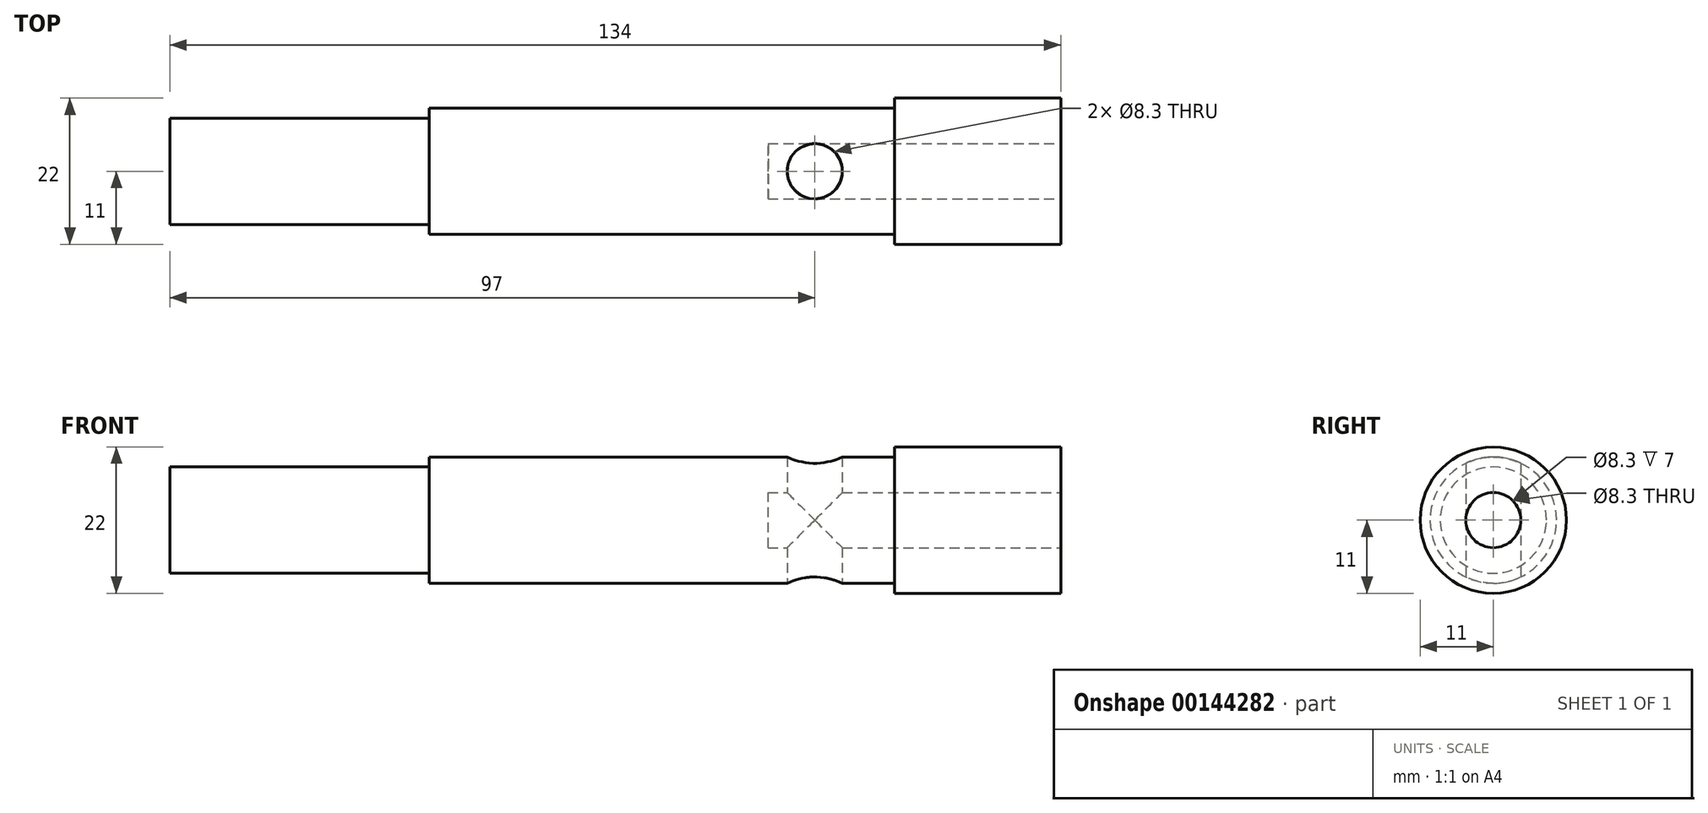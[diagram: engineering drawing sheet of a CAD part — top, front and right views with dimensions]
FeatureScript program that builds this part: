
annotation { "Feature Type Name" : "Feature", "Feature Type Description" : "" }
export const myFeature = defineFeature(function(context is Context, id is Id, definition is map)
    precondition{}
    {
        {
            var Q0;
            Q0=qCreatedBy(makeId("Front.planeOp"),FACE);
            var sketch = newSketch(context, id + "F0", { "sketchPlane" : qUnion([Q0])});
            skLineSegment(sketch, "E0", {"start": v(-58.13, 0) * mm, "end": v(0, 0) * mm, "construction": true});
            skLineSegment(sketch, "E1.bottom", {"start": v(0, 0) * mm, "end": v(-25, 0) * mm});
            skLineSegment(sketch, "E1.top", {"start": v(0, 11) * mm, "end": v(-25, 11) * mm});
            skLineSegment(sketch, "E1.left", {"start": v(0, 0) * mm, "end": v(0, 11) * mm});
            skLineSegment(sketch, "E1.right", {"start": v(-25, 0) * mm, "end": v(-25, 11) * mm});
            skLineSegment(sketch, "E2.bottom", {"start": v(-25, 0) * mm, "end": v(-37, 0) * mm});
            skLineSegment(sketch, "E2.top", {"start": v(-25, 9.5) * mm, "end": v(-37, 9.5) * mm});
            skLineSegment(sketch, "E2.left", {"start": v(-25, 0) * mm, "end": v(-25, 9.5) * mm});
            skLineSegment(sketch, "E2.right", {"start": v(-37, 0) * mm, "end": v(-37, 9.5) * mm});
            skLineSegment(sketch, "E3.bottom", {"start": v(-37, 0) * mm, "end": v(-95, 0) * mm});
            skLineSegment(sketch, "E3.top", {"start": v(-37, 9.5) * mm, "end": v(-95, 9.5) * mm});
            skLineSegment(sketch, "E3.right", {"start": v(-95, 0) * mm, "end": v(-95, 9.5) * mm});
            skLineSegment(sketch, "E4.bottom", {"start": v(-95, 0) * mm, "end": v(-134, 0) * mm});
            skLineSegment(sketch, "E4.top", {"start": v(-95, 8) * mm, "end": v(-134, 8) * mm});
            skLineSegment(sketch, "E4.left", {"start": v(-95, 0) * mm, "end": v(-95, 8) * mm});
            skLineSegment(sketch, "E4.right", {"start": v(-134, 0) * mm, "end": v(-134, 8) * mm});
            skLineSegment(sketch, "E5.MirrorCS", {"start": v(-25, 0) * mm, "end": v(-25, -11) * mm});
            skLineSegment(sketch, "E6.MirrorCS", {"start": v(-37, 0) * mm, "end": v(-37, -9.5) * mm});
            skLineSegment(sketch, "E7.MirrorCS", {"start": v(-95, 0) * mm, "end": v(-95, -8) * mm});
            skLineSegment(sketch, "E8.MirrorCS", {"start": v(-134, 0) * mm, "end": v(-134, -8) * mm});
            skLineSegment(sketch, "E9.MirrorCS", {"start": v(-95, 0) * mm, "end": v(-95, -9.5) * mm});
            skLineSegment(sketch, "E10.MirrorCS", {"start": v(-37, -9.5) * mm, "end": v(-95, -9.5) * mm});
            skLineSegment(sketch, "E11.MirrorCS", {"start": v(-25, 0) * mm, "end": v(-25, -9.5) * mm});
            skLineSegment(sketch, "E12.MirrorCS", {"start": v(-25, -9.5) * mm, "end": v(-37, -9.5) * mm});
            skLineSegment(sketch, "E13.MirrorCS", {"start": v(0, 0) * mm, "end": v(0, -11) * mm});
            skLineSegment(sketch, "E14.MirrorCS", {"start": v(0, -11) * mm, "end": v(-25, -11) * mm});
            skLineSegment(sketch, "E15.MirrorCS", {"start": v(-95, -8) * mm, "end": v(-134, -8) * mm});
            skSolve(sketch);
        }
        {
            var Q0;
            Q0=makeQuery(id+"F0.imprint","IMPRINT",FACE,{"disambiguationData":[TD([[makeQuery(id+"F0.imprint","IMPRINT",EDGE,{"derivedFrom":sQuery(id+"F0.wireOp",EDGE,"E1.bottom")}),-1.0]])]});
            var Q1;
            Q1=makeQuery(id+"F0.imprint","IMPRINT",FACE,{"disambiguationData":[TD([[makeQuery(id+"F0.imprint","IMPRINT",EDGE,{"derivedFrom":sQuery(id+"F0.wireOp",EDGE,"E2.top")}),1.0]])]});
            var Q2;
            Q2=makeQuery(id+"F0.imprint","IMPRINT",FACE,{"disambiguationData":[TD([[makeQuery(id+"F0.imprint","IMPRINT",EDGE,{"derivedFrom":sQuery(id+"F0.wireOp",EDGE,"E3.top")}),1.0]])]});
            var Q3;
            Q3=makeQuery(id+"F0.imprint","IMPRINT",FACE,{"disambiguationData":[TD([[makeQuery(id+"F0.imprint","IMPRINT",EDGE,{"derivedFrom":sQuery(id+"F0.wireOp",EDGE,"E4.top")}),1.0]])]});
            var Q4;
            Q4=sQuery(id+"F0.wireOp",EDGE,"E1.bottom");
            revolve(context, id + "F1", {"entities" : qUnion([Q0, Q1, Q2, Q3]), "axis" : qUnion([Q4]), "revolveType" : RevolveType.FULL});
        }
        {
            var Q0;
            Q0=qCreatedBy(makeId("Top.planeOp"),FACE);
            var sketch = newSketch(context, id + "F2", { "sketchPlane" : qUnion([Q0])});
            skLineSegment(sketch, "E16.0", {"start": v(-37, 0) * mm, "end": v(-95, 0) * mm});
            skLineSegment(sketch, "E17.0", {"start": v(-25, 0) * mm, "end": v(-37, 0) * mm});
            skCircle(sketch, "E18", {"center": v(-37, 0) * mm, "radius": 4.15 * mm});
            skSolve(sketch);
        }
        {
            var Q0;
            {var subQ0=sQuery(id+"F2.wireOp",EDGE,"E17.0");var subQ1=sQuery(id+"F2.wireOp",EDGE,"E16.0");var subQ2=makeQuery(id+"F2.imprint","INTERSECT",VERTEX,{"derivedFrom":[subQ1,subQ0]});Q0=makeQuery(id+"F2.imprint","IMPRINT",FACE,{"disambiguationData":[TD([[makeQuery(id+"F2.imprint","IMPRINT",EDGE,{"disambiguationData":[TD([[subQ2,-1.0]])],"derivedFrom":subQ1}),-1.0]])]});}
            var Q1;
            {var subQ0=sQuery(id+"F2.wireOp",EDGE,"E17.0");var subQ1=sQuery(id+"F2.wireOp",EDGE,"E16.0");var subQ2=makeQuery(id+"F2.imprint","INTERSECT",VERTEX,{"derivedFrom":[subQ1,subQ0]});Q1=makeQuery(id+"F2.imprint","IMPRINT",FACE,{"disambiguationData":[TD([[makeQuery(id+"F2.imprint","IMPRINT",EDGE,{"disambiguationData":[TD([[subQ2,-1.0]])],"derivedFrom":subQ1}),1.0]])]});}
            extrude(context, id + "F3", {"entities" : qUnion([Q0, Q1]), "operationType" : NewBodyOperationType.REMOVE, "endBound" : BoundingType.THROUGH_ALL, "depth" : 25 * mm, "hasSecondDirection" : true, "secondDirectionBound" : SecondDirectionBoundingType.THROUGH_ALL, "secondDirectionOppositeDirection" : true, "secondDirectionDepth" : 25 * mm});
        }
        {
            var Q0;
            Q0=qCreatedBy(makeId("Right.planeOp"),FACE);
            var sketch = newSketch(context, id + "F4", { "sketchPlane" : qUnion([Q0])});
            skCircle(sketch, "E19", {"center": v(0, 0) * mm, "radius": 4.15 * mm});
            skSolve(sketch);
        }
        {
            var Q0;
            Q0 = qSketchRegion(id + "F4", true);
            extrude(context, id + "F5", {"entities" : qUnion([Q0]), "operationType" : NewBodyOperationType.REMOVE, "oppositeDirection" : true, "depth" : 44 * mm});
        }
    });
